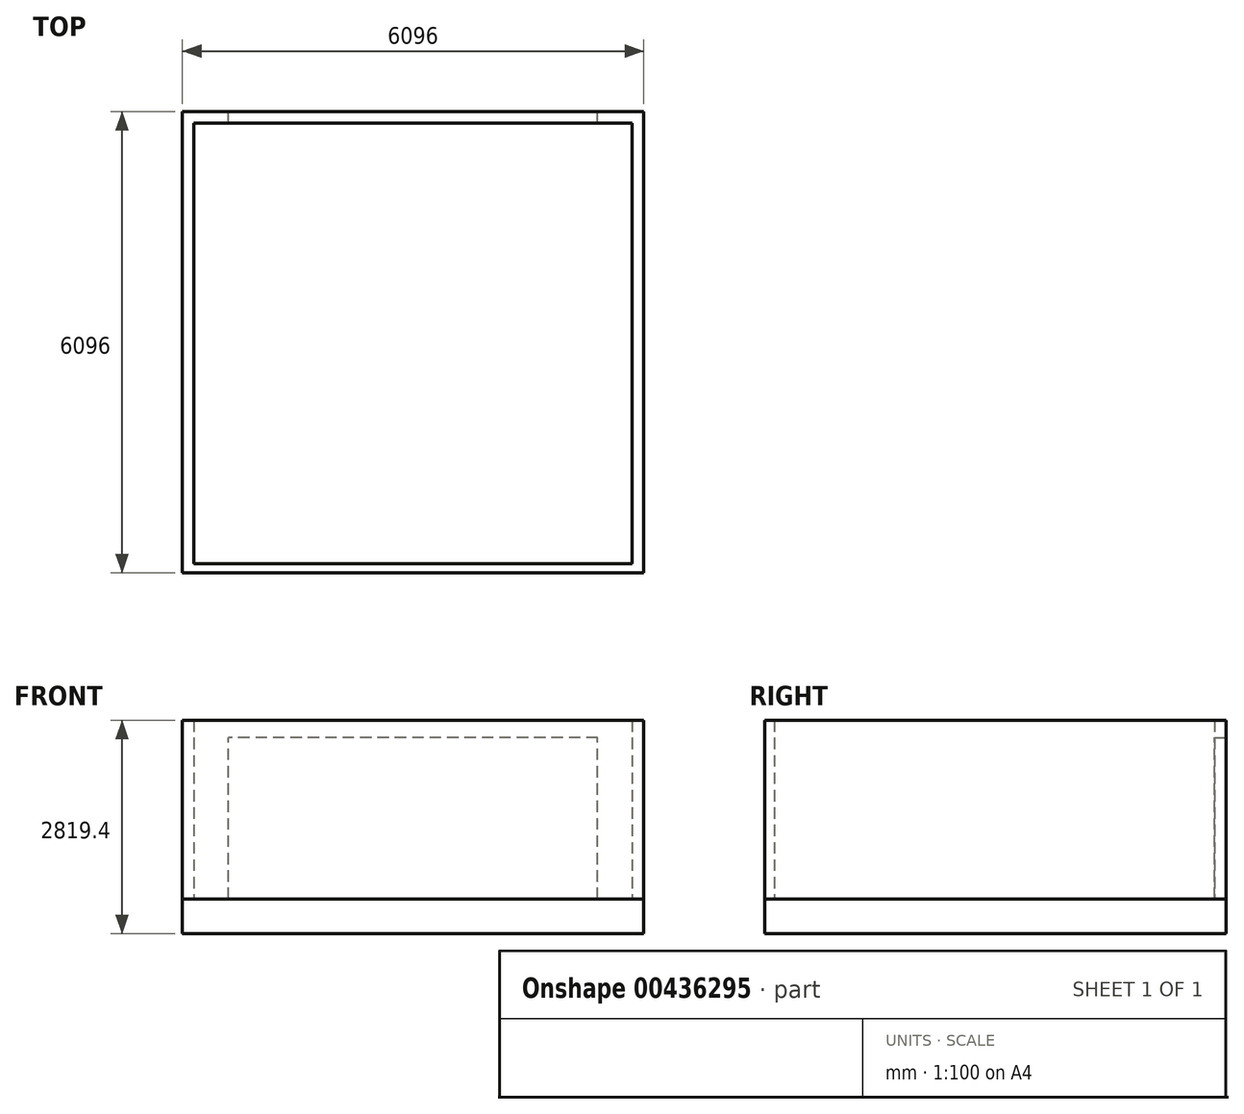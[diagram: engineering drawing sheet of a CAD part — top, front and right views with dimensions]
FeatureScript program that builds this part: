
annotation { "Feature Type Name" : "Feature", "Feature Type Description" : "" }
export const myFeature = defineFeature(function(context is Context, id is Id, definition is map)
    precondition{}
    {
        {
            var Q0;
            Q0=qCreatedBy(makeId("Top.planeOp"),FACE);
            var sketch = newSketch(context, id + "F0", { "sketchPlane" : qUnion([Q0])});
            skLineSegment(sketch, "E0", {"start": v(0, 0) * mm, "end": v(0, 15240) * mm, "construction": true});
            skLineSegment(sketch, "E1", {"start": v(0, 15240) * mm, "end": v(-1524, 15240) * mm, "construction": true});
            skLineSegment(sketch, "E2.bottom", {"start": v(-1524, 15240) * mm, "end": v(-7620, 15240) * mm});
            skLineSegment(sketch, "E2.top", {"start": v(-1524, 21336) * mm, "end": v(-7620, 21336) * mm});
            skLineSegment(sketch, "E2.left", {"start": v(-1524, 15240) * mm, "end": v(-1524, 21336) * mm});
            skLineSegment(sketch, "E2.right", {"start": v(-7620, 15240) * mm, "end": v(-7620, 21336) * mm});
            skSolve(sketch);
        }
        {
            var Q0;
            Q0=makeQuery(id+"F0.imprint","IMPRINT",FACE,{"disambiguationData":[TD([[makeQuery(id+"F0.imprint","IMPRINT",EDGE,{"derivedFrom":sQuery(id+"F0.wireOp",EDGE,"E2.bottom")}),-1.0]])]});
            extrude(context, id + "F1", {"entities" : qUnion([Q0]), "depth" : 457.2 * mm});
        }
        {
            var Q0;
            Q0=makeQuery(id+"F1.opExtrude","CAP_FACE",FACE,{"disambiguationData":[OSD([sQuery(id+"F0.wireOp",EDGE,"E2.bottom"),sQuery(id+"F0.wireOp",EDGE,"E2.top"),sQuery(id+"F0.wireOp",EDGE,"E2.left"),sQuery(id+"F0.wireOp",EDGE,"E2.right")])],"isStart":false});
            var sketch = newSketch(context, id + "F2", { "sketchPlane" : qUnion([Q0])});
            skLineSegment(sketch, "E3.bottom", {"start": v(-1524, 21336) * mm, "end": v(-7620, 21336) * mm});
            skLineSegment(sketch, "E3.top", {"start": v(-1524, 15240) * mm, "end": v(-7620, 15240) * mm});
            skLineSegment(sketch, "E3.left", {"start": v(-1524, 21336) * mm, "end": v(-1524, 15240) * mm});
            skLineSegment(sketch, "E3.right", {"start": v(-7620, 21336) * mm, "end": v(-7620, 15240) * mm});
            skLineSegment(sketch, "E4.top", {"start": v(-1676.4, 15361.92) * mm, "end": v(-7467.6, 15361.92) * mm});
            skLineSegment(sketch, "E4.left", {"start": v(-1676.4, 21183.6) * mm, "end": v(-1676.4, 15361.92) * mm});
            skLineSegment(sketch, "E4.right", {"start": v(-7467.6, 21183.6) * mm, "end": v(-7467.6, 15361.92) * mm});
            skLineSegment(sketch, "E5.trimOffspring", {"start": v(-1676.4, 21183.6) * mm, "end": v(-7467.6, 21183.6) * mm});
            skSolve(sketch);
        }
        {
            var Q0;
            Q0 = qSketchRegion(id + "F2", true);
            extrude(context, id + "F3", {"entities" : qUnion([Q0]), "depth" : 2362.2 * mm});
        }
        {
            var Q0;
            Q0=makeQuery(id+"F3.opExtrude","SWEPT_FACE",FACE,{"disambiguationData":[OSD([sQuery(id+"F2.wireOp",EDGE,"E3.bottom")])]});
            var sketch = newSketch(context, id + "F4", { "sketchPlane" : qUnion([Q0])});
            skLineSegment(sketch, "E6.bottom", {"start": v(2133.6, 457.2) * mm, "end": v(7010.4, 457.2) * mm});
            skLineSegment(sketch, "E6.top", {"start": v(2133.6, 2590.8) * mm, "end": v(7010.4, 2590.8) * mm});
            skLineSegment(sketch, "E6.left", {"start": v(2133.6, 457.2) * mm, "end": v(2133.6, 2590.8) * mm});
            skLineSegment(sketch, "E6.right", {"start": v(7010.4, 457.2) * mm, "end": v(7010.4, 2590.8) * mm});
            skSolve(sketch);
        }
        {
            var Q0;
            Q0 = qSketchRegion(id + "F4", true);
            extrude(context, id + "F5", {"entities" : qUnion([Q0]), "operationType" : NewBodyOperationType.REMOVE, "oppositeDirection" : true, "depth" : 152.4 * mm});
        }
    });
